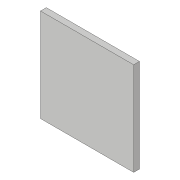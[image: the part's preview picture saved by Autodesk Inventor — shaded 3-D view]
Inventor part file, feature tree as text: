
AUTODESK INVENTOR PART (.ipt)
format: ipt  version: 2019 (Build 230136000, 136)  size: 94,208 bytes
history: native  units: mm
features: sketch x3, extrude x2
ambient origin geometry x8: Origin, YZ Plane, XZ Plane, XY Plane, X Axis, Y Axis, Z Axis, Center Point
bodies: Solid1 (feature_tree)
feature tree (5):
  extrude  "Extrusion1"  Depth=160.0mm
  sketch  "Sketch2"  dims[d2=10.0mm d3=0.0mm d4=10.0mm]
  extrude  "Extrusion2"  Depth=10.0mm
  sketch  "Sketch1"  dims[d0=160.0mm d1=160.0mm]
  sketch  "Sketch3"  dims[d5=80.0mm d6=10.0mm d9=10.0mm d10=0.0mm d11=10.0mm d12=10.0mm d13=140.0mm d14=140.0mm d15=140.0mm d16=10.0mm d17=10.0mm d18=10.0mm d19=10.0mm]
